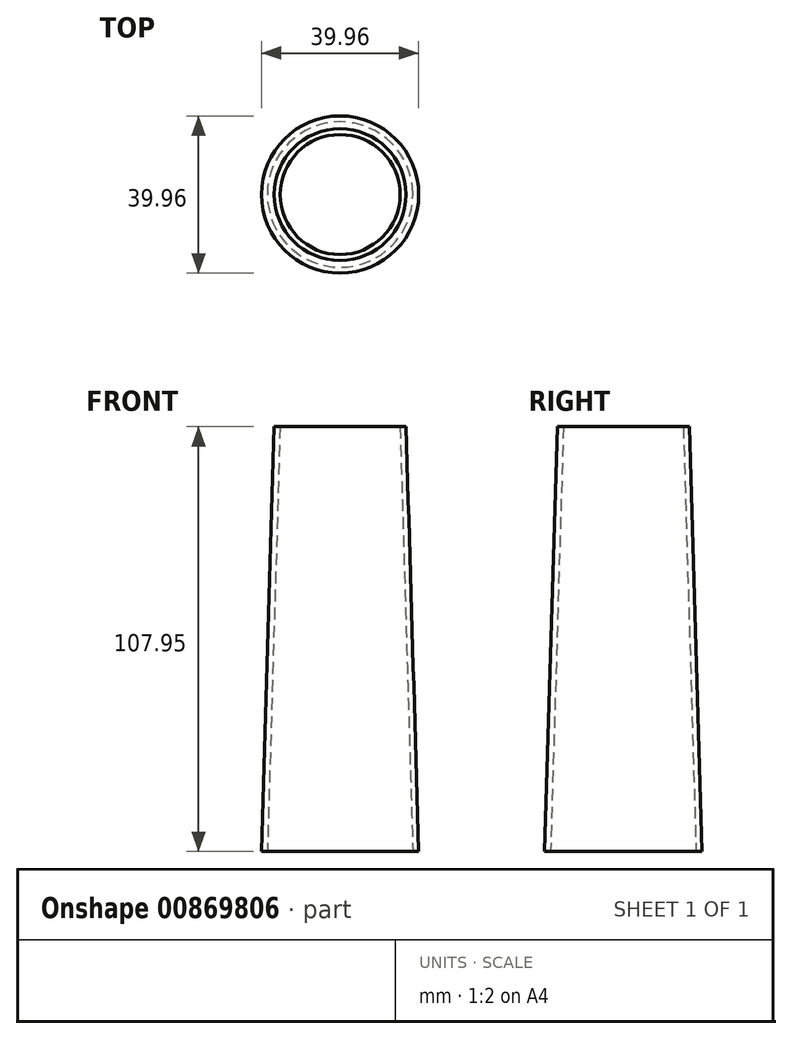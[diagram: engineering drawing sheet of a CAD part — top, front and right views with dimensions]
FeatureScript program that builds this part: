
annotation { "Feature Type Name" : "Feature", "Feature Type Description" : "" }
export const myFeature = defineFeature(function(context is Context, id is Id, definition is map)
    precondition{}
    {
        {
            var Q0;
            Q0=qCreatedBy(makeId("Front.planeOp"),FACE);
            var sketch = newSketch(context, id + "F0", { "sketchPlane" : qUnion([Q0])});
            skLineSegment(sketch, "E0", {"start": v(-15.24, 63.05) * mm, "end": v(-16.74, 63.05) * mm});
            skLineSegment(sketch, "E1", {"start": v(-16.74, 63.05) * mm, "end": v(-19.98, -44.9) * mm});
            skLineSegment(sketch, "E2", {"start": v(-19.98, -44.9) * mm, "end": v(-18.48, -44.9) * mm});
            skLineSegment(sketch, "E3", {"start": v(-18.48, -44.9) * mm, "end": v(-15.24, 63.05) * mm});
            skLineSegment(sketch, "E4", {"start": v(0, 14.77) * mm, "end": v(0, 9.4) * mm});
            skSolve(sketch);
        }
        {
            var Q0;
            Q0=makeQuery(id+"F0.imprint","IMPRINT",FACE,{"disambiguationData":[TD([[makeQuery(id+"F0.imprint","IMPRINT",EDGE,{"derivedFrom":sQuery(id+"F0.wireOp",EDGE,"E0")}),1.0]])]});
            var Q1;
            Q1=sQuery(id+"F0.wireOp",EDGE,"E4");
            revolve(context, id + "F1", {"surfaceOperationType" : NewSurfaceOperationType.NEW, "entities" : qUnion([Q0]), "axis" : qUnion([Q1]), "revolveType" : RevolveType.FULL});
        }
    });
